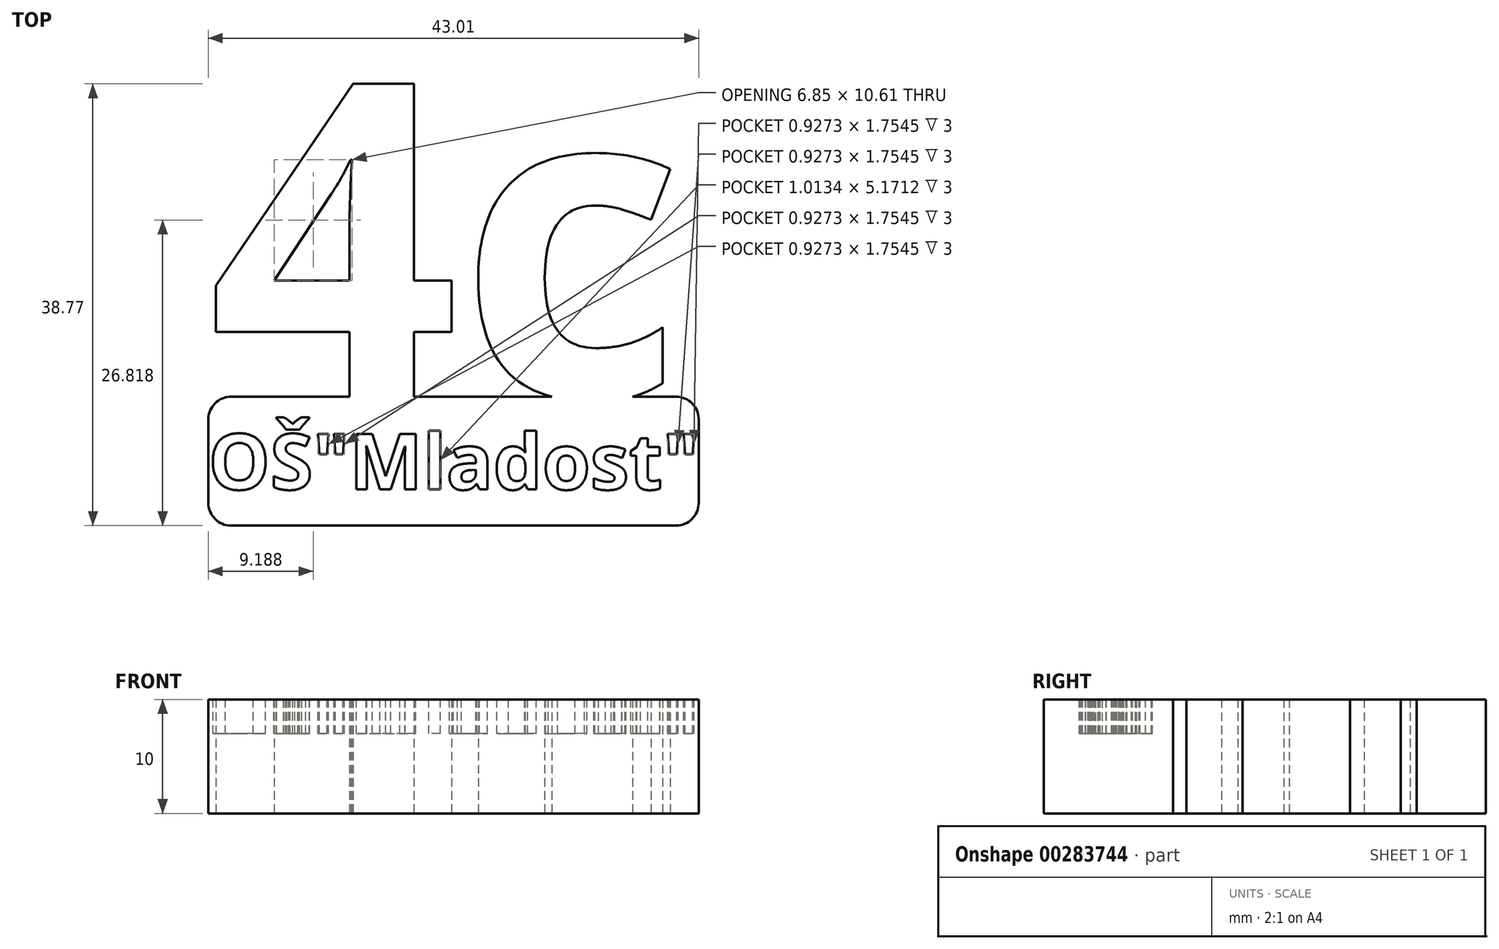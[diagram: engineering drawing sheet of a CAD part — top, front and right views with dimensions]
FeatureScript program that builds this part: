
annotation { "Feature Type Name" : "Feature", "Feature Type Description" : "" }
export const myFeature = defineFeature(function(context is Context, id is Id, definition is map)
    precondition{}
    {
        {
            var Q0;
            Q0=qCreatedBy(makeId("Top.planeOp"),FACE);
            var sketch = newSketch(context, id + "F0", { "sketchPlane" : qUnion([Q0])});
            skText(sketch, "E0", { "text": "4c", "fontName": "OpenSans-Bold.ttf"});
            skLineSegment(sketch, "E1.bottom", {"start": v(0, 0) * mm, "end": v(43, 0) * mm});
            skLineSegment(sketch, "E1.top", {"start": v(0, -11.32) * mm, "end": v(43, -11.32) * mm});
            skLineSegment(sketch, "E1.left", {"start": v(0, 0) * mm, "end": v(0, -11.32) * mm});
            skLineSegment(sketch, "E1.right", {"start": v(43, 0) * mm, "end": v(43, -11.32) * mm});
            const initialGuessF0  = {"E0": [0, 0, 1, 0, 0.02768]};
            skSetInitialGuess(sketch, initialGuessF0);
            skSolve(sketch);
        }
        {
            var Q0;
            Q0=qSketchRegion(id+"F0",true);
            extrude(context, id + "F1", {"entities" : qUnion([Q0]), "depth" : 10 * mm});
        }
        {
            var Q0;
            Q0=makeQuery(id+"F1.opExtrude","CAP_FACE",FACE,{"disambiguationData":[OSD([sQuery(id+"F0.wireOp",EDGE,"E0.sketch_text.stroke-0"),sQuery(id+"F0.wireOp",EDGE,"E0.sketch_text.stroke-1"),sQuery(id+"F0.wireOp",EDGE,"E0.sketch_text.stroke-2"),sQuery(id+"F0.wireOp",EDGE,"E0.sketch_text.stroke-3"),sQuery(id+"F0.wireOp",EDGE,"E0.sketch_text.stroke-4"),sQuery(id+"F0.wireOp",EDGE,"E0.sketch_text.stroke-5"),sQuery(id+"F0.wireOp",EDGE,"E0.sketch_text.stroke-6"),sQuery(id+"F0.wireOp",EDGE,"E0.sketch_text.stroke-7"),sQuery(id+"F0.wireOp",EDGE,"E0.sketch_text.stroke-8"),sQuery(id+"F0.wireOp",EDGE,"E0.sketch_text.stroke-9"),sQuery(id+"F0.wireOp",EDGE,"E0.sketch_text.stroke-10"),sQuery(id+"F0.wireOp",EDGE,"E0.sketch_text.stroke-11"),sQuery(id+"F0.wireOp",EDGE,"E0.sketch_text.stroke-12"),sQuery(id+"F0.wireOp",EDGE,"E0.sketch_text.stroke-13"),sQuery(id+"F0.wireOp",EDGE,"E0.sketch_text.stroke-14"),sQuery(id+"F0.wireOp",EDGE,"E0.sketch_text.stroke-15"),sQuery(id+"F0.wireOp",EDGE,"E0.sketch_text.stroke-16"),sQuery(id+"F0.wireOp",EDGE,"E0.sketch_text.stroke-17"),sQuery(id+"F0.wireOp",EDGE,"E0.sketch_text.stroke-18"),sQuery(id+"F0.wireOp",EDGE,"E0.sketch_text.stroke-19"),sQuery(id+"F0.wireOp",EDGE,"E0.sketch_text.stroke-20"),sQuery(id+"F0.wireOp",EDGE,"E0.sketch_text.stroke-21"),sQuery(id+"F0.wireOp",EDGE,"E0.sketch_text.stroke-22"),sQuery(id+"F0.wireOp",EDGE,"E0.sketch_text.stroke-23"),sQuery(id+"F0.wireOp",EDGE,"E0.sketch_text.stroke-24"),sQuery(id+"F0.wireOp",EDGE,"E0.sketch_text.stroke-25"),sQuery(id+"F0.wireOp",EDGE,"E0.sketch_text.stroke-26"),sQuery(id+"F0.wireOp",EDGE,"E0.sketch_text.stroke-27"),sQuery(id+"F0.wireOp",EDGE,"E0.sketch_text.stroke-28"),sQuery(id+"F0.wireOp",EDGE,"E0.sketch_text.stroke-29"),sQuery(id+"F0.wireOp",EDGE,"E0.sketch_text.stroke-30"),sQuery(id+"F0.wireOp",EDGE,"E0.sketch_text.stroke-31"),sQuery(id+"F0.wireOp",EDGE,"E0.sketch_text.stroke-32"),sQuery(id+"F0.wireOp",EDGE,"E0.sketch_text.stroke-33"),sQuery(id+"F0.wireOp",EDGE,"E0.sketch_text.stroke-34"),sQuery(id+"F0.wireOp",EDGE,"E0.sketch_text.stroke-35"),sQuery(id+"F0.wireOp",EDGE,"E0.sketch_text.stroke-36"),sQuery(id+"F0.wireOp",EDGE,"E0.sketch_text.stroke-37"),sQuery(id+"F0.wireOp",EDGE,"E0.sketch_text.stroke-38"),sQuery(id+"F0.wireOp",EDGE,"E0.sketch_text.stroke-39"),sQuery(id+"F0.wireOp",EDGE,"E1.bottom"),sQuery(id+"F0.wireOp",EDGE,"E1.top"),sQuery(id+"F0.wireOp",EDGE,"E1.left"),sQuery(id+"F0.wireOp",EDGE,"E1.right")])],"isStart":false});
            var sketch = newSketch(context, id + "F2", { "sketchPlane" : qUnion([Q0])});
            skText(sketch, "E2", { "text": "OŠ\"Mladost\"", "fontName": "OpenSans-Bold.ttf"});
            const initialGuessF2  = {"E2": [0, -0.00815, 1, 0, 0.0049]};
            skSetInitialGuess(sketch, initialGuessF2);
            skSolve(sketch);
        }
        {
            var Q0;
            Q0=qSketchRegion(id+"F2",true);
            extrude(context, id + "F3", {"entities" : qUnion([Q0]), "operationType" : NewBodyOperationType.REMOVE, "oppositeDirection" : true, "depth" : 3 * mm});
        }
        {
            var Q0;
            Q0=makeQuery(id+"F1.opExtrude","SWEPT_EDGE",EDGE,{"disambiguationData":[OSD([sQuery(id+"F0.wireOp",EDGE,"E1.top"),sQuery(id+"F0.wireOp",EDGE,"E1.right")])]});
            var Q1;
            Q1=makeQuery(id+"F1.opExtrude","SWEPT_EDGE",EDGE,{"disambiguationData":[OSD([sQuery(id+"F0.wireOp",EDGE,"E1.top"),sQuery(id+"F0.wireOp",EDGE,"E1.left")])]});
            var Q2;
            Q2=makeQuery(id+"F1.opExtrude","SWEPT_EDGE",EDGE,{"disambiguationData":[OSD([sQuery(id+"F0.wireOp",EDGE,"E1.bottom"),sQuery(id+"F0.wireOp",EDGE,"E1.left")])]});
            var Q3;
            Q3=makeQuery(id+"F1.opExtrude","SWEPT_EDGE",EDGE,{"disambiguationData":[OSD([sQuery(id+"F0.wireOp",EDGE,"E1.bottom"),sQuery(id+"F0.wireOp",EDGE,"E1.right")])]});
            fillet(context, id + "F4", {"entities" : qUnion([Q0, Q1, Q2, Q3]), "radius" : 2 * mm, "tangentPropagation" : true, "allowEdgeOverflow" : false});
        }
    });
